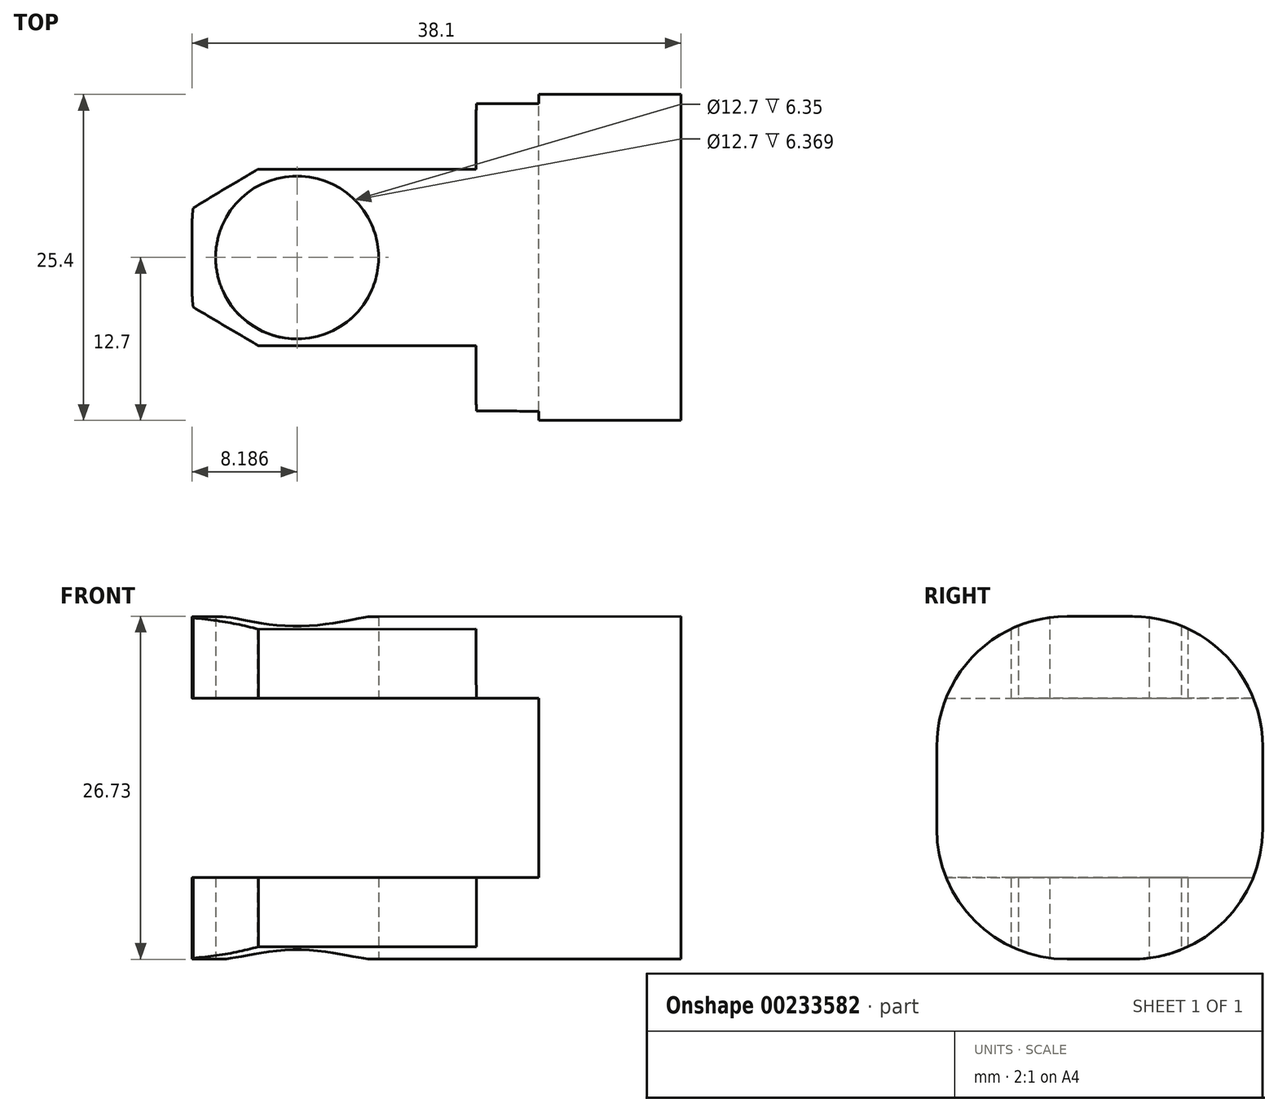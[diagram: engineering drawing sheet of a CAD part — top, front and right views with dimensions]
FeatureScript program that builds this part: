
annotation { "Feature Type Name" : "Feature", "Feature Type Description" : "" }
export const myFeature = defineFeature(function(context is Context, id is Id, definition is map)
    precondition{}
    {
        {
            var Q0;
            Q0=qCreatedBy(makeId("Front.planeOp"),FACE);
            var sketch = newSketch(context, id + "F0", { "sketchPlane" : qUnion([Q0])});
            skLineSegment(sketch, "E0.bottom", {"start": v(19.05, -6.98) * mm, "end": v(0, -6.99) * mm});
            skLineSegment(sketch, "E0.top", {"start": v(19.05, 6.99) * mm, "end": v(0, 6.99) * mm});
            skPoint(sketch, "E0.middle", {"position": v(0, 0) * mm});
            skLineSegment(sketch, "E1", {"start": v(0, 6.99) * mm, "end": v(0, 13.34) * mm});
            skLineSegment(sketch, "E2", {"start": v(0, -6.99) * mm, "end": v(0, -13.33) * mm});
            skLineSegment(sketch, "E3", {"start": v(0, -13.33) * mm, "end": v(38.1, -13.33) * mm});
            skLineSegment(sketch, "E4", {"start": v(38.1, -13.33) * mm, "end": v(38.1, 13.39) * mm});
            skLineSegment(sketch, "E5", {"start": v(38.1, 13.39) * mm, "end": v(0, 13.34) * mm});
            skPoint(sketch, "E0.right.end.orphan", {"position": v(-19.05, 6.99) * mm});
            skPoint(sketch, "E6.orphan", {"position": v(-19.05, -6.99) * mm});
            skLineSegment(sketch, "E7", {"start": v(19.05, 6.99) * mm, "end": v(27, 6.99) * mm});
            skLineSegment(sketch, "E8", {"start": v(27, 6.99) * mm, "end": v(27, -8.58) * mm});
            skLineSegment(sketch, "E9", {"start": v(19.05, -6.98) * mm, "end": v(27, -6.98) * mm});
            skSolve(sketch);
        }
        {
            var Q0;
            Q0=qSketchRegion(id+"F0",true);
            extrude(context, id + "F1", {"entities" : qUnion([Q0]), "depth" : 25.4 * mm});
        }
        {
            var Q0;
            Q0=makeQuery(id+"F1.opExtrude","SWEPT_FACE",FACE,{"disambiguationData":[OSD([sQuery(id+"F0.wireOp",EDGE,"E3")])]});
            var sketch = newSketch(context, id + "F2", { "sketchPlane" : qUnion([Q0])});
            skCircle(sketch, "E10", {"center": v(8.19, 12.7) * mm, "radius": 6.35 * mm});
            skPoint(sketch, "E10.centerSnap0", {"position": v(0, 12.7) * mm});
            skSolve(sketch);
        }
        {
            var Q0;
            Q0=makeQuery(id+"F1.opExtrude","CAP_EDGE",EDGE,{"disambiguationData":[OSD([sQuery(id+"F0.wireOp",EDGE,"E2")])],"isStart":true});
            var Q1;
            Q1=makeQuery(id+"F1.opExtrude","CAP_EDGE",EDGE,{"disambiguationData":[OSD([sQuery(id+"F0.wireOp",EDGE,"E1")])],"isStart":true});
            var Q2;
            Q2=makeQuery(id+"F1.opExtrude","CAP_EDGE",EDGE,{"disambiguationData":[OSD([sQuery(id+"F0.wireOp",EDGE,"E1")])],"isStart":false});
            var Q3;
            Q3=makeQuery(id+"F1.opExtrude","CAP_EDGE",EDGE,{"disambiguationData":[OSD([sQuery(id+"F0.wireOp",EDGE,"E2")])],"isStart":false});
            fillet(context, id + "F3", {"entities" : qUnion([Q0, Q1, Q2, Q3]), "radius" : 10.16 * mm, "tangentPropagation" : true, "allowEdgeOverflow" : false});
        }
        {
            var Q0;
            Q0=makeQuery(id+"F2.imprint","IMPRINT",FACE,{"disambiguationData":[TD([[makeQuery(id+"F2.imprint","IMPRINT",EDGE,{"derivedFrom":sQuery(id+"F2.wireOp",EDGE,"E10")}),1.0]])]});
            extrude(context, id + "F4", {"entities" : qUnion([Q0]), "operationType" : NewBodyOperationType.REMOVE, "endBound" : BoundingType.THROUGH_ALL, "oppositeDirection" : true, "depth" : 25.4 * mm});
        }
        {
            var Q0;
            Q0=makeQuery(id+"F1.opExtrude","SWEPT_FACE",FACE,{"disambiguationData":[OSD([sQuery(id+"F0.wireOp",EDGE,"E5")])]});
            var sketch = newSketch(context, id + "F5", { "sketchPlane" : qUnion([Q0])});
            skLineSegment(sketch, "E11.bottom", {"start": v(22.15, -5.82) * mm, "end": v(-18.45, -5.82) * mm});
            skLineSegment(sketch, "E11.top", {"start": v(22.15, -19.58) * mm, "end": v(-18.45, -19.58) * mm});
            skLineSegment(sketch, "E11.left", {"start": v(22.15, -5.82) * mm, "end": v(22.15, -19.58) * mm});
            skLineSegment(sketch, "E11.right", {"start": v(-18.45, -5.82) * mm, "end": v(-18.45, -19.58) * mm});
            skPoint(sketch, "E11.middle", {"position": v(1.85, -12.7) * mm});
            skLineSegment(sketch, "E12", {"start": v(22.15, -19.58) * mm, "end": v(22.15, -25.4) * mm});
            skLineSegment(sketch, "E13", {"start": v(22.15, -5.82) * mm, "end": v(22.15, 0) * mm});
            skLineSegment(sketch, "E14", {"start": v(-6.3, -19.58) * mm, "end": v(17.98, -30.66) * mm});
            skLineSegment(sketch, "E15", {"start": v(17.98, -30.66) * mm, "end": v(22.15, -25.4) * mm});
            skLineSegment(sketch, "E16", {"start": v(-7.33, -5.82) * mm, "end": v(20.42, 6.01) * mm});
            skLineSegment(sketch, "E17", {"start": v(20.42, 6.01) * mm, "end": v(22.15, 0) * mm});
            skSolve(sketch);
        }
        {
            var Q0;
            {var subQ7=sQuery(id+"F5.wireOp",EDGE,"E16");Q0=makeQuery(id+"F5.imprint","IMPRINT",FACE,{"disambiguationData":[TD([[makeQuery(id+"F5.imprint","IMPRINT",EDGE,{"derivedFrom":subQ7}),-1.0]])]});}
            var Q1;
            {var subQ0=sQuery(id+"F5.wireOp",EDGE,"E13");Q1=makeQuery(id+"F5.imprint","IMPRINT",FACE,{"disambiguationData":[TD([[makeQuery(id+"F5.imprint","IMPRINT",EDGE,{"derivedFrom":subQ0}),1.0]])]});}
            var Q2;
            {var subQ0=sQuery(id+"F5.wireOp",EDGE,"E12");Q2=makeQuery(id+"F5.imprint","IMPRINT",FACE,{"disambiguationData":[TD([[makeQuery(id+"F5.imprint","IMPRINT",EDGE,{"derivedFrom":subQ0}),-1.0]])]});}
            var Q3;
            {var subQ6=sQuery(id+"F5.wireOp",EDGE,"E14");Q3=makeQuery(id+"F5.imprint","IMPRINT",FACE,{"disambiguationData":[TD([[makeQuery(id+"F5.imprint","IMPRINT",EDGE,{"derivedFrom":subQ6}),1.0]])]});}
            extrude(context, id + "F6", {"entities" : qUnion([Q0, Q1, Q2, Q3]), "operationType" : NewBodyOperationType.REMOVE, "endBound" : BoundingType.THROUGH_ALL, "oppositeDirection" : true, "depth" : 25.4 * mm});
        }
        {
            var Q0;
            Q0=makeQuery(id+"F1.opExtrude","CAP_EDGE",EDGE,{"disambiguationData":[OSD([sQuery(id+"F0.wireOp",EDGE,"E5")])],"isStart":false});
            var Q1;
            Q1=makeQuery(id+"F1.opExtrude","CAP_EDGE",EDGE,{"disambiguationData":[OSD([sQuery(id+"F0.wireOp",EDGE,"E5")])],"isStart":true});
            var Q2;
            Q2=makeQuery(id+"F1.opExtrude","CAP_EDGE",EDGE,{"disambiguationData":[OSD([sQuery(id+"F0.wireOp",EDGE,"E3")])],"isStart":true});
            var Q3;
            Q3=makeQuery(id+"F1.opExtrude","CAP_EDGE",EDGE,{"disambiguationData":[OSD([sQuery(id+"F0.wireOp",EDGE,"E3")])],"isStart":false});
            fillet(context, id + "F7", {"entities" : qUnion([Q0, Q1, Q2, Q3]), "radius" : 10.16 * mm, "tangentPropagation" : true, "allowEdgeOverflow" : false});
        }
        {
            var Q0;
            Q0=qCreatedBy(makeId("Top.planeOp"),FACE);
            var sketch = newSketch(context, id + "F8", { "sketchPlane" : qUnion([Q0])});
            skLineSegment(sketch, "E18", {"start": v(6.35, -5.07) * mm, "end": v(-2.7, -10.52) * mm});
            skLineSegment(sketch, "E19", {"start": v(-2.7, -10.52) * mm, "end": v(-2.7, -14.92) * mm});
            skLineSegment(sketch, "E20", {"start": v(-2.7, -14.92) * mm, "end": v(6.35, -20.28) * mm});
            skLineSegment(sketch, "E21", {"start": v(6.35, -20.28) * mm, "end": v(-5.74, -20.28) * mm});
            skLineSegment(sketch, "E22", {"start": v(-5.74, -20.28) * mm, "end": v(-5.74, -5.07) * mm});
            skLineSegment(sketch, "E23", {"start": v(-5.74, -5.07) * mm, "end": v(6.35, -5.07) * mm});
            skSolve(sketch);
        }
        {
            var Q0;
            Q0=makeQuery(id+"F8.imprint","IMPRINT",FACE,{"disambiguationData":[TD([[makeQuery(id+"F8.imprint","IMPRINT",EDGE,{"derivedFrom":sQuery(id+"F8.wireOp",EDGE,"E18")}),-1.0]])]});
            extrude(context, id + "F9", {"entities" : qUnion([Q0]), "operationType" : NewBodyOperationType.REMOVE, "endBound" : BoundingType.SYMMETRIC, "oppositeDirection" : true, "depth" : 101.6 * mm});
        }
    });
